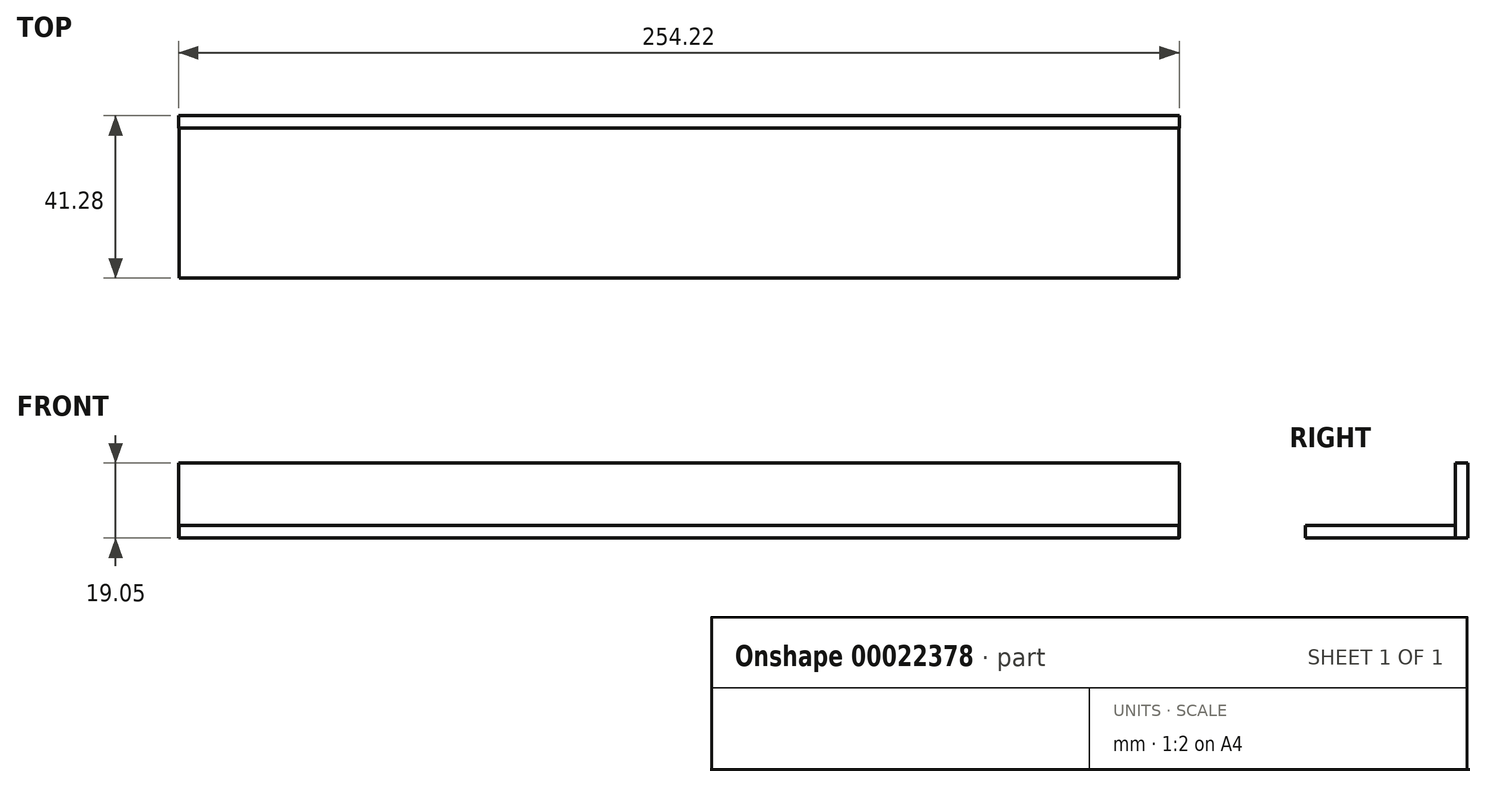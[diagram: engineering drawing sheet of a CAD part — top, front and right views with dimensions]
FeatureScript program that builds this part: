
annotation { "Feature Type Name" : "Feature", "Feature Type Description" : "" }
export const myFeature = defineFeature(function(context is Context, id is Id, definition is map)
    precondition{}
    {
        {
            var Q0;
            Q0=qCreatedBy(makeId("Front.planeOp"),FACE);
            var sketch = newSketch(context, id + "F0", { "sketchPlane" : qUnion([Q0])});
            skLineSegment(sketch, "E0.bottom", {"start": v(-135.14, -23.38) * mm, "end": v(118.86, -23.38) * mm});
            skLineSegment(sketch, "E0.top", {"start": v(-135.14, -26.55) * mm, "end": v(118.86, -26.55) * mm});
            skLineSegment(sketch, "E0.left", {"start": v(-135.14, -23.38) * mm, "end": v(-135.14, -26.55) * mm});
            skLineSegment(sketch, "E0.right", {"start": v(118.86, -23.38) * mm, "end": v(118.86, -26.55) * mm});
            skSolve(sketch);
        }
        {
            var Q0;
            Q0=makeQuery(id+"F0.imprint","IMPRINT",FACE,{"disambiguationData":[TD([[makeQuery(id+"F0.imprint","IMPRINT",EDGE,{"derivedFrom":sQuery(id+"F0.wireOp",EDGE,"E0.bottom")}),-1.0]])]});
            extrude(context, id + "F1", {"entities" : qUnion([Q0]), "depth" : 38.1 * mm});
        }
        {
            var Q0;
            Q0=qCreatedBy(makeId("Right.planeOp"),FACE);
            var sketch = newSketch(context, id + "F2", { "sketchPlane" : qUnion([Q0])});
            skLineSegment(sketch, "E1.bottom", {"start": v(0, -26.55) * mm, "end": v(3.17, -26.55) * mm});
            skLineSegment(sketch, "E1.top", {"start": v(0, -7.5) * mm, "end": v(3.17, -7.5) * mm});
            skLineSegment(sketch, "E1.left", {"start": v(0, -26.55) * mm, "end": v(0, -7.5) * mm});
            skLineSegment(sketch, "E1.right", {"start": v(3.18, -26.55) * mm, "end": v(3.18, -7.5) * mm});
            skSolve(sketch);
        }
        {
            var Q0;
            Q0=makeQuery(id+"F2.imprint","IMPRINT",FACE,{"disambiguationData":[TD([[makeQuery(id+"F2.imprint","IMPRINT",EDGE,{"derivedFrom":sQuery(id+"F2.wireOp",EDGE,"E1.bottom")}),1.0]])]});
            extrude(context, id + "F3", {"entities" : qUnion([Q0]), "operationType" : NewBodyOperationType.ADD, "oppositeDirection" : true, "depth" : 135.32 * mm, "hasSecondDirection" : true, "secondDirectionOppositeDirection" : false, "secondDirectionDepth" : 118.9 * mm});
        }
    });
